# Revit family: Mixer-Bath Shower-Stylus In Wall Body
name_source: partatom
category: Plumbing Fixtures
revit_build: Autodesk Revit MEP 2014 (Build: 20140709_2115(x64)
units: mm (PartAtom-declared; Revit-internal decimal feet)

## types (1)
- Chrome
    Assembly Code = D2020300
    CW Connection = Yes
    CWFU = 0
    ConnectorDiameter = 20 mm  [stored 0.0656168 ft]
    Cost = 0 $
    Default Elevation = 1000 mm  [stored 3.28084 ft]
    HW Connection = Yes
    HWFU = 0
    Manufacturer = GWA Bathrooms&Kitchens
    Material_ANZRS = Metal-Chrome-Caroma
    Model = 632209C
    ModifiedIssue_ANZRS = 20161018.54 $
    Type Comments = Stylus Bath/Shower Mixer In Wall Body
    URL = http://specify.caroma.com.au
    Vent Connection = No
    Waste Connection = No

note: [stored X ft] marks values corroborated as IEEE doubles in the binary element streams (Revit-internal decimal feet)

## geometry (parser evidence)
native form markers: Sweep x1
no freeform markers — native parametric forms only
